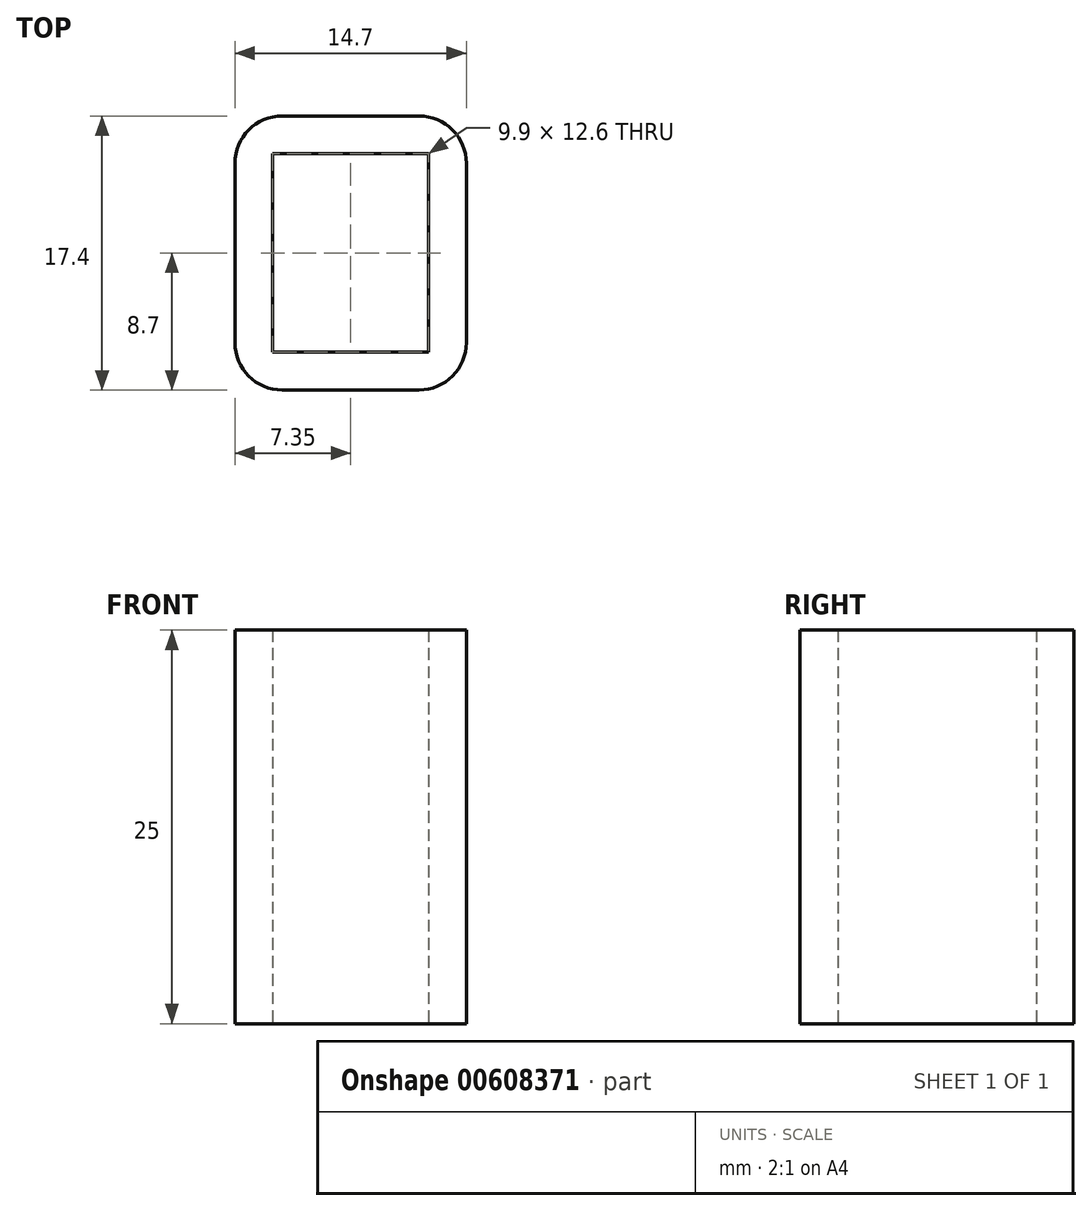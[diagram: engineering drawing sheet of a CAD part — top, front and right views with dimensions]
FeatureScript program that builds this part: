
annotation { "Feature Type Name" : "Feature", "Feature Type Description" : "" }
export const myFeature = defineFeature(function(context is Context, id is Id, definition is map)
    precondition{}
    {
        {
            var Q0;
            Q0=qCreatedBy(makeId("Top.planeOp"),FACE);
            var sketch = newSketch(context, id + "F0", { "sketchPlane" : qUnion([Q0])});
            skLineSegment(sketch, "E0.bottom", {"start": v(4.95, -6.3) * mm, "end": v(-4.95, -6.3) * mm});
            skLineSegment(sketch, "E0.top", {"start": v(4.95, 6.3) * mm, "end": v(-4.95, 6.3) * mm});
            skLineSegment(sketch, "E0.left", {"start": v(4.95, -6.3) * mm, "end": v(4.95, 6.3) * mm});
            skLineSegment(sketch, "E0.right", {"start": v(-4.95, -6.3) * mm, "end": v(-4.95, 6.3) * mm});
            skPoint(sketch, "E0.middle", {"position": v(0, 0) * mm});
            skLineSegment(sketch, "E1.bottom", {"start": v(7.35, -8.7) * mm, "end": v(-7.35, -8.7) * mm});
            skLineSegment(sketch, "E1.top", {"start": v(7.35, 8.7) * mm, "end": v(-7.35, 8.7) * mm});
            skLineSegment(sketch, "E1.left", {"start": v(7.35, -8.7) * mm, "end": v(7.35, 8.7) * mm});
            skLineSegment(sketch, "E1.right", {"start": v(-7.35, -8.7) * mm, "end": v(-7.35, 8.7) * mm});
            skSolve(sketch);
        }
        {
            var Q0;
            Q0 = qSketchRegion(id + "F0", true);
            extrude(context, id + "F1", {"entities" : qUnion([Q0]), "depth" : 25 * mm, "offsetDistance" : 25 * mm});
        }
        {
            var Q0;
            Q0=makeQuery(id+"F1.opExtrude","SWEPT_EDGE",EDGE,{"disambiguationData":[OSD([sQuery(id+"F0.wireOp",EDGE,"E1.bottom"),sQuery(id+"F0.wireOp",EDGE,"E1.right")])]});
            var Q1;
            Q1=makeQuery(id+"F1.opExtrude","SWEPT_EDGE",EDGE,{"disambiguationData":[OSD([sQuery(id+"F0.wireOp",EDGE,"E1.bottom"),sQuery(id+"F0.wireOp",EDGE,"E1.left")])]});
            var Q2;
            Q2=makeQuery(id+"F1.opExtrude","SWEPT_EDGE",EDGE,{"disambiguationData":[OSD([sQuery(id+"F0.wireOp",EDGE,"E1.top"),sQuery(id+"F0.wireOp",EDGE,"E1.left")])]});
            var Q3;
            Q3=makeQuery(id+"F1.opExtrude","SWEPT_EDGE",EDGE,{"disambiguationData":[OSD([sQuery(id+"F0.wireOp",EDGE,"E1.top"),sQuery(id+"F0.wireOp",EDGE,"E1.right")])]});
            fillet(context, id + "F2", {"entities" : qUnion([Q0, Q1, Q2, Q3]), "radius" : 3 * mm, "tangentPropagation" : true, "allowEdgeOverflow" : false});
        }
    });
